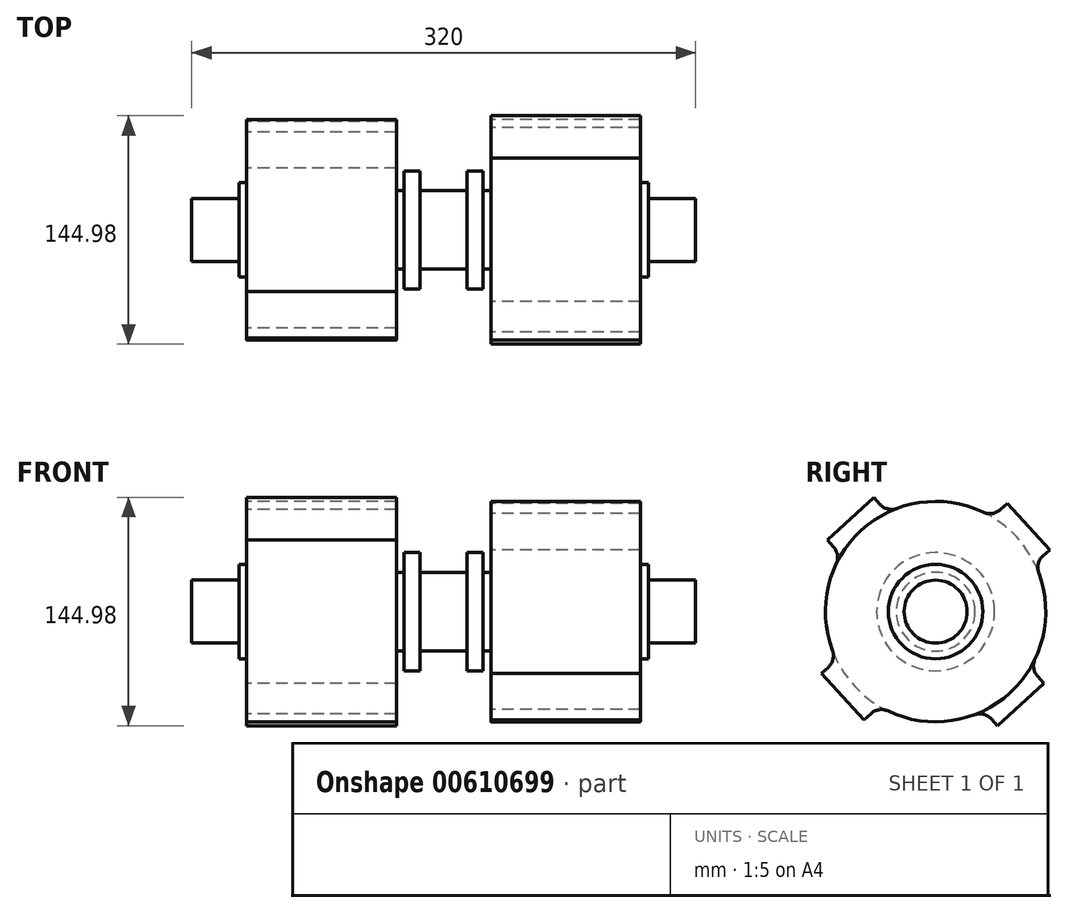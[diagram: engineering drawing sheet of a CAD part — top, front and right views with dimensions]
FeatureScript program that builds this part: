
annotation { "Feature Type Name" : "Feature", "Feature Type Description" : "" }
export const myFeature = defineFeature(function(context is Context, id is Id, definition is map)
    precondition{}
    {
        {
            var Q0;
            Q0=qCreatedBy(makeId("Right.planeOp"),FACE);
            var sketch = newSketch(context, id + "F0", { "sketchPlane" : qUnion([Q0])});
            skCircle(sketch, "E0", {"center": v(0, 0) * mm, "radius": 30 * mm});
            skSolve(sketch);
        }
        {
            var Q0;
            Q0=makeQuery(id+"F0.imprint","IMPRINT",FACE,{"disambiguationData":[TD([[makeQuery(id+"F0.imprint","IMPRINT",EDGE,{"derivedFrom":sQuery(id+"F0.wireOp",EDGE,"E0")}),1.0]])]});
            extrude(context, id + "F1", {"entities" : qUnion([Q0]), "depth" : 5 * mm, "offsetDistance" : 25 * mm});
        }
        {
            var Q0;
            Q0=makeQuery(id+"F1.opExtrude","CAP_FACE",FACE,{"disambiguationData":[OSD([sQuery(id+"F0.wireOp",EDGE,"E0")])],"isStart":false});
            var sketch = newSketch(context, id + "F2", { "sketchPlane" : qUnion([Q0])});
            skCircle(sketch, "E1", {"center": v(0, 0) * mm, "radius": 70 * mm});
            skLineSegment(sketch, "E2", {"start": v(-68.8, 45.46) * mm, "end": v(39.31, -72.49) * mm});
            skLineSegment(sketch, "E3", {"start": v(39.31, -72.49) * mm, "end": v(68.8, -45.46) * mm});
            skLineSegment(sketch, "E4", {"start": v(68.8, -45.46) * mm, "end": v(-39.31, 72.49) * mm});
            skLineSegment(sketch, "E5", {"start": v(-39.31, 72.49) * mm, "end": v(-68.8, 45.46) * mm});
            skSolve(sketch);
        }
        {
            var Q0;
            Q0 = qSketchRegion(id + "F2", true);
            extrude(context, id + "F3", {"entities" : qUnion([Q0]), "operationType" : NewBodyOperationType.ADD, "depth" : 95 * mm, "offsetDistance" : 25 * mm});
        }
        {
            var Q0;
            Q0=makeQuery(id+"F3.opExtrude","CAP_FACE",FACE,{"disambiguationData":[OSD([sQuery(id+"F2.wireOp",EDGE,"E1"),sQuery(id+"F2.wireOp",EDGE,"E2"),sQuery(id+"F2.wireOp",EDGE,"E3"),sQuery(id+"F2.wireOp",EDGE,"E4"),sQuery(id+"F2.wireOp",EDGE,"E5")])],"isStart":false});
            var sketch = newSketch(context, id + "F4", { "sketchPlane" : qUnion([Q0])});
            skCircle(sketch, "E6", {"center": v(0, 0) * mm, "radius": 25 * mm});
            skSolve(sketch);
        }
        {
            var Q0;
            Q0=makeQuery(id+"F4.imprint","IMPRINT",FACE,{"disambiguationData":[TD([[makeQuery(id+"F4.imprint","IMPRINT",EDGE,{"derivedFrom":sQuery(id+"F4.wireOp",EDGE,"E6")}),1.0]])]});
            extrude(context, id + "F5", {"entities" : qUnion([Q0]), "operationType" : NewBodyOperationType.ADD, "depth" : 5 * mm, "offsetDistance" : 25 * mm});
        }
        {
            var Q0;
            Q0=makeQuery(id+"F5.opExtrude","CAP_FACE",FACE,{"disambiguationData":[OSD([sQuery(id+"F4.wireOp",EDGE,"E6")])],"isStart":false});
            var sketch = newSketch(context, id + "F6", { "sketchPlane" : qUnion([Q0])});
            skCircle(sketch, "E7", {"center": v(0, 0) * mm, "radius": 37.5 * mm});
            skSolve(sketch);
        }
        {
            var Q0;
            Q0=makeQuery(id+"F6.imprint","IMPRINT",FACE,{"disambiguationData":[TD([[makeQuery(id+"F6.imprint","IMPRINT",EDGE,{"derivedFrom":sQuery(id+"F6.wireOp",EDGE,"E7")}),1.0]])]});
            var Q1;
            Q1=makeQuery(id+"F6.imprint","IMPRINT",FACE,{"disambiguationData":[TD([[makeQuery(id+"F6.imprint","IMPRINT",EDGE,{"derivedFrom":makeQuery(id+"F5.opExtrude","CAP_EDGE",EDGE,{"disambiguationData":[OSD([sQuery(id+"F4.wireOp",EDGE,"E6")])],"isStart":false})}),1.0]])]});
            extrude(context, id + "F7", {"entities" : qUnion([Q0, Q1]), "operationType" : NewBodyOperationType.ADD, "depth" : 10 * mm, "offsetDistance" : 25 * mm});
        }
        {
            var Q0;
            Q0=makeQuery(id+"F7.opExtrude","CAP_FACE",FACE,{"disambiguationData":[OSD([sQuery(id+"F6.wireOp",EDGE,"E7")])],"isStart":false});
            var sketch = newSketch(context, id + "F8", { "sketchPlane" : qUnion([Q0])});
            skCircle(sketch, "E8", {"center": v(0, 0) * mm, "radius": 25 * mm});
            skSolve(sketch);
        }
        {
            var Q0;
            Q0 = qSketchRegion(id + "F8", true);
            extrude(context, id + "F9", {"entities" : qUnion([Q0]), "operationType" : NewBodyOperationType.ADD, "depth" : 30 * mm, "offsetDistance" : 25 * mm});
        }
        {
            var Q0;
            Q0=makeQuery(id+"F9.opExtrude","CAP_FACE",FACE,{"disambiguationData":[OSD([sQuery(id+"F8.wireOp",EDGE,"E8")])],"isStart":false});
            var sketch = newSketch(context, id + "F10", { "sketchPlane" : qUnion([Q0])});
            skCircle(sketch, "E9", {"center": v(0, 0) * mm, "radius": 37.5 * mm});
            skSolve(sketch);
        }
        {
            var Q0;
            Q0 = qSketchRegion(id + "F10", true);
            extrude(context, id + "F11", {"entities" : qUnion([Q0]), "operationType" : NewBodyOperationType.ADD, "depth" : 10 * mm, "offsetDistance" : 25 * mm});
        }
        {
            var Q0;
            Q0=makeQuery(id+"F11.opExtrude","CAP_FACE",FACE,{"disambiguationData":[OSD([sQuery(id+"F10.wireOp",EDGE,"E9")])],"isStart":false});
            var sketch = newSketch(context, id + "F12", { "sketchPlane" : qUnion([Q0])});
            skCircle(sketch, "E10", {"center": v(0, 0) * mm, "radius": 25 * mm});
            skSolve(sketch);
        }
        {
            var Q0;
            Q0 = qSketchRegion(id + "F12", true);
            extrude(context, id + "F13", {"entities" : qUnion([Q0]), "operationType" : NewBodyOperationType.ADD, "depth" : 5 * mm, "offsetDistance" : 25 * mm});
        }
        {
            var Q0;
            Q0=makeQuery(id+"F13.opExtrude","CAP_FACE",FACE,{"disambiguationData":[OSD([sQuery(id+"F12.wireOp",EDGE,"E10")])],"isStart":false});
            var sketch = newSketch(context, id + "F14", { "sketchPlane" : qUnion([Q0])});
            skLineSegment(sketch, "E11", {"start": v(45.46, 68.8) * mm, "end": v(72.49, 39.31) * mm});
            skLineSegment(sketch, "E12", {"start": v(72.49, 39.31) * mm, "end": v(-45.46, -68.8) * mm});
            skLineSegment(sketch, "E13", {"start": v(-45.46, -68.8) * mm, "end": v(-72.49, -39.31) * mm});
            skLineSegment(sketch, "E14", {"start": v(-72.49, -39.31) * mm, "end": v(45.46, 68.8) * mm});
            skCircle(sketch, "E15", {"center": v(0, 0) * mm, "radius": 70 * mm});
            skSolve(sketch);
        }
        {
            var Q0;
            Q0 = qSketchRegion(id + "F14", true);
            extrude(context, id + "F15", {"entities" : qUnion([Q0]), "operationType" : NewBodyOperationType.ADD, "depth" : 95 * mm, "offsetDistance" : 25 * mm});
        }
        {
            var Q0;
            Q0=makeQuery(id+"F15.opExtrude","CAP_FACE",FACE,{"disambiguationData":[OSD([sQuery(id+"F14.wireOp",EDGE,"E11"),sQuery(id+"F14.wireOp",EDGE,"E12"),sQuery(id+"F14.wireOp",EDGE,"E13"),sQuery(id+"F14.wireOp",EDGE,"E14"),sQuery(id+"F14.wireOp",EDGE,"E15")])],"isStart":false});
            var sketch = newSketch(context, id + "F16", { "sketchPlane" : qUnion([Q0])});
            skCircle(sketch, "E16", {"center": v(0, 0) * mm, "radius": 30 * mm});
            skSolve(sketch);
        }
        {
            var Q0;
            Q0 = qSketchRegion(id + "F16", true);
            extrude(context, id + "F17", {"entities" : qUnion([Q0]), "operationType" : NewBodyOperationType.ADD, "depth" : 5 * mm, "offsetDistance" : 25 * mm});
        }
        {
            var Q0;
            Q0=makeQuery(id+"F1.opExtrude","CAP_FACE",FACE,{"disambiguationData":[OSD([sQuery(id+"F0.wireOp",EDGE,"E0")])],"isStart":true});
            var sketch = newSketch(context, id + "F18", { "sketchPlane" : qUnion([Q0])});
            skCircle(sketch, "E17", {"center": v(0, 0) * mm, "radius": 20 * mm});
            skSolve(sketch);
        }
        {
            var Q0;
            Q0=makeQuery(id+"F18.imprint","IMPRINT",FACE,{"disambiguationData":[TD([[makeQuery(id+"F18.imprint","IMPRINT",EDGE,{"derivedFrom":sQuery(id+"F18.wireOp",EDGE,"E17")}),1.0]])]});
            extrude(context, id + "F19", {"entities" : qUnion([Q0]), "operationType" : NewBodyOperationType.ADD, "depth" : 30 * mm, "offsetDistance" : 25 * mm});
        }
        {
            var Q0;
            Q0=makeQuery(id+"F17.opExtrude","CAP_FACE",FACE,{"disambiguationData":[OSD([sQuery(id+"F16.wireOp",EDGE,"E16")])],"isStart":false});
            var sketch = newSketch(context, id + "F20", { "sketchPlane" : qUnion([Q0])});
            skCircle(sketch, "E18", {"center": v(0, 0) * mm, "radius": 20 * mm});
            skSolve(sketch);
        }
        {
            var Q0;
            Q0=makeQuery(id+"F20.imprint","IMPRINT",FACE,{"disambiguationData":[TD([[makeQuery(id+"F20.imprint","IMPRINT",EDGE,{"derivedFrom":sQuery(id+"F20.wireOp",EDGE,"E18")}),1.0]])]});
            extrude(context, id + "F21", {"entities" : qUnion([Q0]), "operationType" : NewBodyOperationType.ADD, "depth" : 30 * mm, "offsetDistance" : 25 * mm});
        }
        {
            var Q0;
            {var subQ0=sQuery(id+"F2.wireOp",EDGE,"E2");var subQ1=sQuery(id+"F2.wireOp",EDGE,"E1");Q0=makeQuery(id+"F3.opExtrude","SWEPT_EDGE",EDGE,{"disambiguationData":[OSD([subQ1,subQ0]),TDD([makeQuery(id+"F2.imprint","INTERSECT",VERTEX,{"disambiguationData":[OD(0.0)],"derivedFrom":[subQ1,subQ0]})])]});}
            var Q1;
            {var subQ0=sQuery(id+"F14.wireOp",EDGE,"E15");var subQ1=sQuery(id+"F14.wireOp",EDGE,"E14");Q1=makeQuery(id+"F15.opExtrude","SWEPT_EDGE",EDGE,{"disambiguationData":[OSD([subQ1,subQ0]),TDD([makeQuery(id+"F14.imprint","INTERSECT",VERTEX,{"disambiguationData":[OD(0.0)],"derivedFrom":[subQ1,subQ0]})])]});}
            var Q2;
            {var subQ0=sQuery(id+"F2.wireOp",EDGE,"E4");var subQ1=sQuery(id+"F2.wireOp",EDGE,"E1");Q2=makeQuery(id+"F3.opExtrude","SWEPT_EDGE",EDGE,{"disambiguationData":[OSD([subQ1,subQ0]),TDD([makeQuery(id+"F2.imprint","INTERSECT",VERTEX,{"disambiguationData":[OD(0.0)],"derivedFrom":[subQ1,subQ0]})])]});}
            var Q3;
            {var subQ0=sQuery(id+"F14.wireOp",EDGE,"E15");var subQ1=sQuery(id+"F14.wireOp",EDGE,"E14");Q3=makeQuery(id+"F15.opExtrude","SWEPT_EDGE",EDGE,{"disambiguationData":[OSD([subQ1,subQ0]),TDD([makeQuery(id+"F14.imprint","INTERSECT",VERTEX,{"disambiguationData":[OD(1.0)],"derivedFrom":[subQ1,subQ0]})])]});}
            var Q4;
            {var subQ0=sQuery(id+"F14.wireOp",EDGE,"E15");var subQ1=sQuery(id+"F14.wireOp",EDGE,"E12");Q4=makeQuery(id+"F15.opExtrude","SWEPT_EDGE",EDGE,{"disambiguationData":[OSD([subQ1,subQ0]),TDD([makeQuery(id+"F14.imprint","INTERSECT",VERTEX,{"disambiguationData":[OD(0.0)],"derivedFrom":[subQ1,subQ0]})])]});}
            var Q5;
            {var subQ0=sQuery(id+"F2.wireOp",EDGE,"E4");var subQ1=sQuery(id+"F2.wireOp",EDGE,"E1");Q5=makeQuery(id+"F3.opExtrude","SWEPT_EDGE",EDGE,{"disambiguationData":[OSD([subQ1,subQ0]),TDD([makeQuery(id+"F2.imprint","INTERSECT",VERTEX,{"disambiguationData":[OD(1.0)],"derivedFrom":[subQ1,subQ0]})])]});}
            var Q6;
            {var subQ0=sQuery(id+"F2.wireOp",EDGE,"E2");var subQ1=sQuery(id+"F2.wireOp",EDGE,"E1");Q6=makeQuery(id+"F3.opExtrude","SWEPT_EDGE",EDGE,{"disambiguationData":[OSD([subQ1,subQ0]),TDD([makeQuery(id+"F2.imprint","INTERSECT",VERTEX,{"disambiguationData":[OD(1.0)],"derivedFrom":[subQ1,subQ0]})])]});}
            var Q7;
            {var subQ0=sQuery(id+"F14.wireOp",EDGE,"E15");var subQ1=sQuery(id+"F14.wireOp",EDGE,"E12");Q7=makeQuery(id+"F15.opExtrude","SWEPT_EDGE",EDGE,{"disambiguationData":[OSD([subQ1,subQ0]),TDD([makeQuery(id+"F14.imprint","INTERSECT",VERTEX,{"disambiguationData":[OD(1.0)],"derivedFrom":[subQ1,subQ0]})])]});}
            fillet(context, id + "F22", {"entities" : qUnion([Q0, Q1, Q2, Q3, Q4, Q5, Q6, Q7]), "radius" : 10 * mm, "tangentPropagation" : true, "allowEdgeOverflow" : false});
        }
    });
